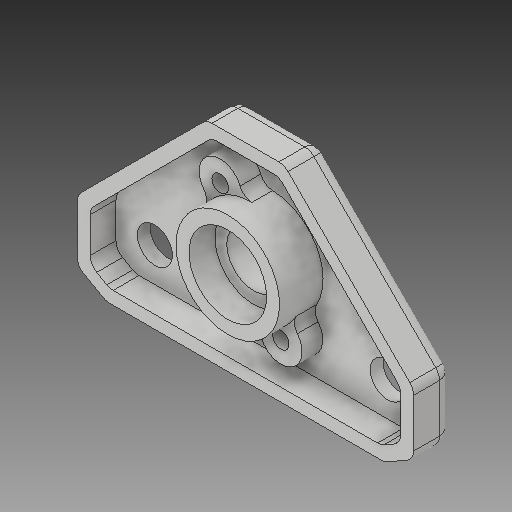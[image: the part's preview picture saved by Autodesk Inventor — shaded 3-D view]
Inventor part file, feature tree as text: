
AUTODESK INVENTOR PART (.ipt)
format: ipt  version: 2017 (Build 210142000, 142)  size: 203,776 bytes
history: native  units: in
note: dims shown in document units (in); Inventor stores cm internally (conversion verified against a paired STEP export)
features: fillet x1
ambient origin geometry x8: Origin, YZ Plane, XZ Plane, XY Plane, X Axis, Y Axis, Z Axis, Center Point
bodies: Solid1 (feature_tree)
feature tree (1):
  fillet  "Fillet2"  [1 undecoded]
note: 1 required parameter value undecoded (feature->parameter linkage not recoverable at this tier; creation-order binding heuristic only, values carry confidence <= 0.55)
